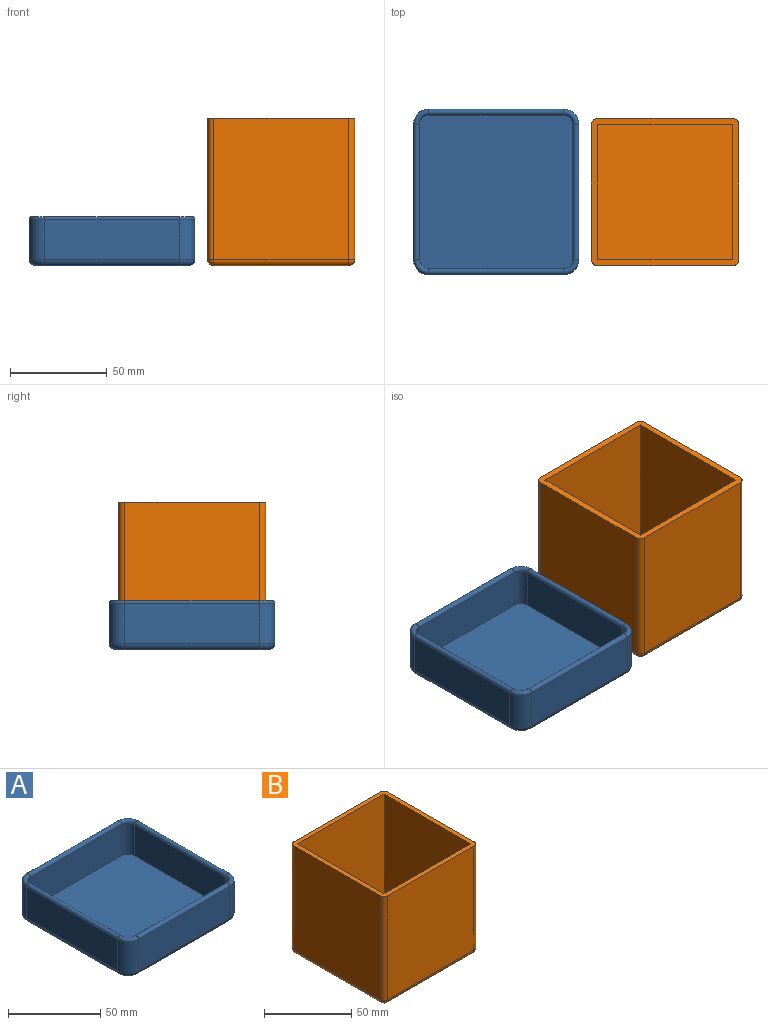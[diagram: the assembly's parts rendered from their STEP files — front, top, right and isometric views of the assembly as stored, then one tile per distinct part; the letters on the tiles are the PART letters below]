
ASSEMBLY  parts=2 mates=1
PART A: 34 faces, bbox 87x87x25.4 mm
  f0: plane 69.85x20.64mm, normal (-1,0,0), area 1441.5mm2, adj f1,f7,f21,f33
  f1: cylinder r=7.94mm len=20.64mm, axis (0,0,-1), area 257.3mm2, adj f0,f2,f19,f32
  f2: plane 69.85x20.64mm, normal (0,-1,0), area 1441.5mm2, adj f1,f3,f18,f30
  f3: cylinder r=7.94mm len=20.64mm, axis (0,0,-1), area 257.3mm2, adj f2,f4,f20,f28
  f4: plane 69.85x20.64mm, normal (1,0,0), area 1441.5mm2, adj f3,f5,f22,f26
  f5: cylinder r=7.94mm len=20.64mm, axis (0,0,-1), area 257.3mm2, adj f4,f6,f24,f27
  f6: plane 69.85x20.64mm, normal (0,1,0), area 1441.5mm2, adj f5,f7,f25,f29
  f7: cylinder r=7.94mm len=20.64mm, axis (0,0,-1), area 257.3mm2, adj f0,f6,f23,f31
  f8: plane 79.38x79.38mm, normal (0,0,-1), area 6280.9mm2, adj f18,f19,f20,f21,f22,f23,f24,f25
  f9: plane 69.85x20.64mm, normal (1,0,0), area 1441.5mm2, adj f10,f16,f17,f33
  f10: cylinder r=4.76mm len=20.64mm, axis (0,0,-1), area 154.4mm2, adj f9,f11,f17,f32
  f11: plane 69.85x20.64mm, normal (0,1,0), area 1441.5mm2, adj f10,f12,f17,f30
  f12: cylinder r=4.76mm len=20.64mm, axis (0,0,-1), area 154.4mm2, adj f11,f13,f17,f28
  f13: plane 69.85x20.64mm, normal (-1,0,0), area 1441.5mm2, adj f12,f14,f17,f26
  f14: cylinder r=4.76mm len=20.64mm, axis (0,0,-1), area 154.4mm2, adj f13,f15,f17,f27
  f15: plane 69.85x20.64mm, normal (0,-1,0), area 1441.5mm2, adj f14,f16,f17,f29
  f16: cylinder r=4.76mm len=20.64mm, axis (0,0,-1), area 154.4mm2, adj f9,f15,f17,f31
  f17: plane 79.38x79.38mm, normal (0,0,1), area 6280.9mm2, adj f9,f10,f11,f12,f13,f14,f15,f16
  f18: cylinder r=3.17mm len=69.85mm, axis (1,0,0), area 348.4mm2, adj f2,f8,f19,f20
  f19: torus R=4.76mm, axis (0,0,1), area 53.1mm2, adj f1,f8,f18,f21
  f20: torus R=4.76mm, axis (0,0,1), area 53.1mm2, adj f3,f8,f18,f22
  f21: cylinder r=3.17mm len=69.85mm, axis (0,-1,0), area 348.4mm2, adj f0,f8,f19,f23
  f22: cylinder r=3.17mm len=69.85mm, axis (0,1,0), area 348.4mm2, adj f4,f8,f20,f24
  f23: torus R=4.76mm, axis (0,0,1), area 53.1mm2, adj f7,f8,f21,f25
  f24: torus R=4.76mm, axis (0,0,1), area 53.1mm2, adj f5,f8,f22,f25
  f25: cylinder r=3.17mm len=69.85mm, axis (-1,0,0), area 348.4mm2, adj f6,f8,f23,f24
  f26: cylinder r=1.59mm len=69.85mm, axis (0,-1,0), area 348.4mm2, adj f4,f13,f27,f28
  f27: torus R=6.35mm, axis (0,0,1), area 49.7mm2, adj f5,f14,f26,f29
  f28: torus R=6.35mm, axis (0,0,1), area 49.7mm2, adj f3,f12,f26,f30
  f29: cylinder r=1.59mm len=69.85mm, axis (1,0,0), area 348.4mm2, adj f6,f15,f27,f31
  f30: cylinder r=1.59mm len=69.85mm, axis (-1,0,0), area 348.4mm2, adj f2,f11,f28,f32
  f31: torus R=6.35mm, axis (0,0,1), area 49.7mm2, adj f7,f16,f29,f33
  f32: torus R=6.35mm, axis (0,0,1), area 49.7mm2, adj f1,f10,f30,f33
  f33: cylinder r=1.59mm len=69.85mm, axis (0,1,0), area 348.4mm2, adj f0,f9,f31,f32
PART B: 23 faces, bbox 76.2x76.2x76.2 mm
  f0: plane 76.2x76.2mm, normal (0,0,1), area 918.8mm2, adj f1,f2,f3,f4,f6,f8,f11,f17
  f1: plane 73.03x69.85mm, normal (0,1,0), area 5100.8mm2, adj f0,f11,f15,f17
  f2: plane 73.03x69.85mm, normal (-1,0,0), area 5100.8mm2, adj f0,f8,f14,f17
  f3: plane 73.03x69.85mm, normal (0,-1,0), area 5100.8mm2, adj f0,f6,f8,f9
  f4: plane 73.03x69.85mm, normal (1,0,0), area 5100.8mm2, adj f0,f6,f10,f11
  f5: plane 69.85x69.85mm, normal (0,0,-1), area 4879mm2, adj f9,f10,f14,f15
  f6: cylinder r=3.17mm len=73.03mm, axis (0,0,1), area 364.2mm2, adj f0,f3,f4,f7
  f7: sphere r=3.17mm, area 15.8mm2, adj f6,f9,f10
  f8: cylinder r=3.17mm len=73.03mm, axis (0,0,-1), area 364.2mm2, adj f0,f2,f3,f12
  f9: cylinder r=3.17mm len=69.85mm, axis (1,0,0), area 348.4mm2, adj f3,f5,f7,f12
  f10: cylinder r=3.17mm len=69.85mm, axis (0,1,0), area 348.4mm2, adj f4,f5,f7,f13
  f11: cylinder r=3.17mm len=73.03mm, axis (0,0,-1), area 364.2mm2, adj f0,f1,f4,f13
  f12: sphere r=3.17mm, area 15.8mm2, adj f8,f9,f14
  f13: sphere r=3.17mm, area 15.8mm2, adj f10,f11,f15
  f14: cylinder r=3.17mm len=69.85mm, axis (0,-1,0), area 348.4mm2, adj f2,f5,f12,f16
  f15: cylinder r=3.17mm len=69.85mm, axis (-1,0,0), area 348.4mm2, adj f1,f5,f13,f16
  f16: sphere r=3.17mm, area 15.8mm2, adj f14,f15,f17
  f17: cylinder r=3.17mm len=73.03mm, axis (0,0,1), area 364.2mm2, adj f0,f1,f2,f16
  f18: plane 73.03x69.85mm, normal (0,-1,0), area 5100.8mm2, adj f0,f19,f21,f22
  f19: plane 73.03x69.85mm, normal (1,0,0), area 5100.8mm2, adj f0,f18,f20,f22
  f20: plane 73.03x69.85mm, normal (0,1,0), area 5100.8mm2, adj f0,f19,f21,f22
  f21: plane 73.03x69.85mm, normal (-1,0,0), area 5100.8mm2, adj f0,f18,f20,f22
  f22: plane 69.85x69.85mm, normal (0,0,1), area 4879mm2, adj f18,f19,f20,f21
PLACE A t=(-114.8,59.69,-31.57)mm
PLACE B t=(-23.37,50.08,-31.57)mm
MATE planar B.f5 <-> A.f8  axis (0,0,-1) through (-23.37,50.08,-31.57)mm
